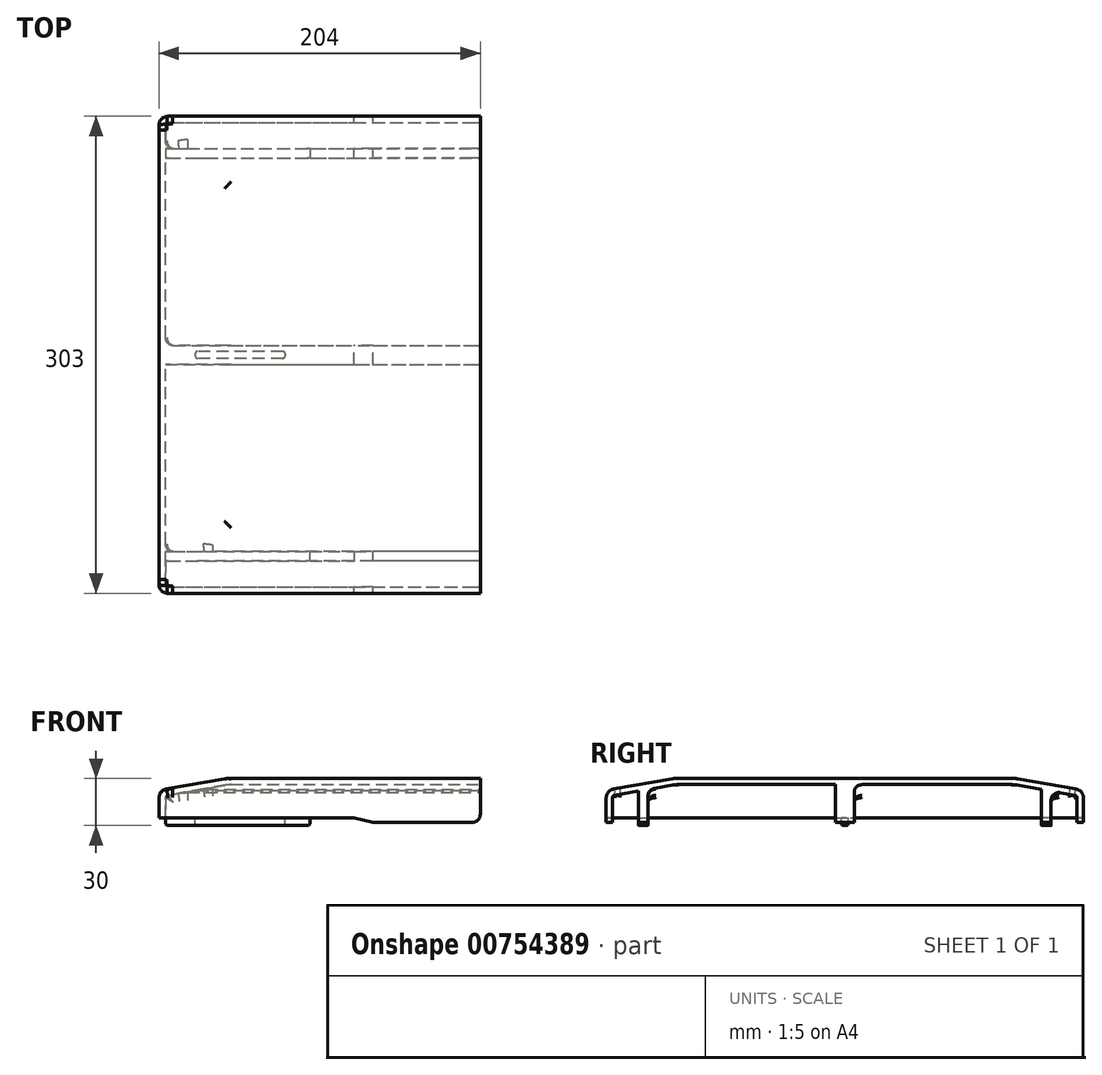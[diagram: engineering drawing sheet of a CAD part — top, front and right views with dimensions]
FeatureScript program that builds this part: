
annotation { "Feature Type Name" : "Feature", "Feature Type Description" : "" }
export const myFeature = defineFeature(function(context is Context, id is Id, definition is map)
    precondition{}
    {
        {
            var Q0;
            Q0=qCreatedBy(makeId("Front.planeOp"),FACE);
            var sketch = newSketch(context, id + "F0", { "sketchPlane" : qUnion([Q0])});
            skLineSegment(sketch, "E0.bottom", {"start": v(0, 0) * mm, "end": v(200, 0) * mm});
            skLineSegment(sketch, "E0.top", {"start": v(0, 21) * mm, "end": v(200, 21) * mm});
            skLineSegment(sketch, "E0.left", {"start": v(0, 0) * mm, "end": v(0, 21) * mm});
            skLineSegment(sketch, "E0.right", {"start": v(200, 0) * mm, "end": v(200, 21) * mm});
            skSolve(sketch);
        }
        {
            var Q0;
            Q0=makeQuery(id+"F0.imprint","IMPRINT",FACE,{"disambiguationData":[TD([[makeQuery(id+"F0.imprint","IMPRINT",EDGE,{"derivedFrom":sQuery(id+"F0.wireOp",EDGE,"E0.bottom")}),1.0]])]});
            extrude(context, id + "F1", {"entities" : qUnion([Q0]), "endBound" : BoundingType.SYMMETRIC, "depth" : 295 * mm, "offsetDistance" : 25 * mm});
        }
        {
            var Q0;
            Q0=makeQuery(id+"F1.opExtrude","CAP_EDGE",EDGE,{"disambiguationData":[OSD([sQuery(id+"F0.wireOp",EDGE,"E0.top")])],"isStart":false});
            var Q1;
            Q1=makeQuery(id+"F1.opExtrude","SWEPT_EDGE",EDGE,{"disambiguationData":[OSD([sQuery(id+"F0.wireOp",EDGE,"E0.top"),sQuery(id+"F0.wireOp",EDGE,"E0.left")])]});
            var Q2;
            Q2=makeQuery(id+"F1.opExtrude","CAP_EDGE",EDGE,{"disambiguationData":[OSD([sQuery(id+"F0.wireOp",EDGE,"E0.top")])],"isStart":true});
            chamfer(context, id + "F2", {"entities" : qUnion([Q0, Q1, Q2]), "chamferType" : ChamferType.TWO_OFFSETS, "width1" : 40 * mm, "oppositeDirection" : false, "width2" : 7 * mm, "tangentPropagation" : true});
        }
        {
            var Q0;
            {var subQ0=sQuery(id+"F0.wireOp",EDGE,"E0.top");Q0=makeQuery(id+"F2.opChamfer","BLEND_EDGE",EDGE,{"blendedFrom":[makeQuery(id+"F1.opExtrude","CAP_EDGE",EDGE,{"disambiguationData":[OSD([subQ0])],"isStart":false}),makeQuery(id+"F1.opExtrude","SWEPT_FACE",FACE,{"disambiguationData":[OSD([subQ0])]})],"blendedInto":[makeQuery(id+"F1.opExtrude","SWEPT_FACE",FACE,{"disambiguationData":[OSD([subQ0])]})]});}
            var Q1;
            {var subQ0=sQuery(id+"F0.wireOp",EDGE,"E0.top");Q1=makeQuery(id+"F2.opChamfer","BLEND_EDGE",EDGE,{"blendedFrom":[makeQuery(id+"F1.opExtrude","CAP_EDGE",EDGE,{"disambiguationData":[OSD([subQ0])],"isStart":true}),makeQuery(id+"F1.opExtrude","SWEPT_FACE",FACE,{"disambiguationData":[OSD([subQ0])]})],"blendedInto":[makeQuery(id+"F1.opExtrude","SWEPT_FACE",FACE,{"disambiguationData":[OSD([subQ0])]})]});}
            var Q2;
            {var subQ0=sQuery(id+"F0.wireOp",EDGE,"E0.top");Q2=makeQuery(id+"F2.opChamfer","BLEND_EDGE",EDGE,{"blendedFrom":[makeQuery(id+"F1.opExtrude","SWEPT_EDGE",EDGE,{"disambiguationData":[OSD([subQ0,sQuery(id+"F0.wireOp",EDGE,"E0.left")])]}),makeQuery(id+"F1.opExtrude","CAP_EDGE",EDGE,{"disambiguationData":[OSD([subQ0])],"isStart":false})],"blendedInto":[]});}
            var Q3;
            {var subQ0=sQuery(id+"F0.wireOp",EDGE,"E0.top");Q3=makeQuery(id+"F2.opChamfer","BLEND_EDGE",EDGE,{"blendedFrom":[makeQuery(id+"F1.opExtrude","SWEPT_EDGE",EDGE,{"disambiguationData":[OSD([subQ0,sQuery(id+"F0.wireOp",EDGE,"E0.left")])]}),makeQuery(id+"F1.opExtrude","CAP_EDGE",EDGE,{"disambiguationData":[OSD([subQ0])],"isStart":true})],"blendedInto":[]});}
            var Q4;
            {var subQ0=sQuery(id+"F0.wireOp",EDGE,"E0.top");Q4=makeQuery(id+"F2.opChamfer","BLEND_EDGE",EDGE,{"blendedFrom":[makeQuery(id+"F1.opExtrude","SWEPT_EDGE",EDGE,{"disambiguationData":[OSD([subQ0,sQuery(id+"F0.wireOp",EDGE,"E0.left")])]}),makeQuery(id+"F1.opExtrude","SWEPT_FACE",FACE,{"disambiguationData":[OSD([subQ0])]})],"blendedInto":[makeQuery(id+"F1.opExtrude","SWEPT_FACE",FACE,{"disambiguationData":[OSD([subQ0])]})]});}
            fillet(context, id + "F3", {"entities" : qUnion([Q0, Q1, Q2, Q3, Q4]), "radius" : 20 * mm, "tangentPropagation" : true, "allowEdgeOverflow" : false});
        }
        {
            var Q0;
            Q0=makeQuery(id+"F1.opExtrude","CAP_EDGE",EDGE,{"disambiguationData":[OSD([sQuery(id+"F0.wireOp",EDGE,"E0.left")])],"isStart":false});
            var Q1;
            {var subQ0=sQuery(id+"F0.wireOp",EDGE,"E0.left");var subQ1=sQuery(id+"F0.wireOp",EDGE,"E0.top");Q1=makeQuery(id+"F3.opFillet","BLEND_EDGE",EDGE,{"blendedFrom":[makeQuery(id+"F2.opChamfer","BLEND_EDGE",EDGE,{"blendedFrom":[makeQuery(id+"F1.opExtrude","SWEPT_EDGE",EDGE,{"disambiguationData":[OSD([subQ1,subQ0])]}),makeQuery(id+"F1.opExtrude","CAP_EDGE",EDGE,{"disambiguationData":[OSD([subQ1])],"isStart":false})],"blendedInto":[]}),makeQuery(id+"F1.opExtrude","CAP_FACE",FACE,{"disambiguationData":[OSD([sQuery(id+"F0.wireOp",EDGE,"E0.bottom"),subQ1,subQ0,sQuery(id+"F0.wireOp",EDGE,"E0.right")])],"isStart":false})],"blendedInto":[makeQuery(id+"F1.opExtrude","CAP_FACE",FACE,{"disambiguationData":[OSD([sQuery(id+"F0.wireOp",EDGE,"E0.bottom"),subQ1,subQ0,sQuery(id+"F0.wireOp",EDGE,"E0.right")])],"isStart":false})]});}
            var Q2;
            {var subQ0=sQuery(id+"F0.wireOp",EDGE,"E0.left");Q2=makeQuery(id+"F2.opChamfer","BLEND_EDGE",EDGE,{"blendedFrom":[makeQuery(id+"F1.opExtrude","SWEPT_EDGE",EDGE,{"disambiguationData":[OSD([sQuery(id+"F0.wireOp",EDGE,"E0.top"),subQ0])]}),makeQuery(id+"F1.opExtrude","SWEPT_FACE",FACE,{"disambiguationData":[OSD([subQ0])]})],"blendedInto":[makeQuery(id+"F1.opExtrude","SWEPT_FACE",FACE,{"disambiguationData":[OSD([subQ0])]})]});}
            var Q3;
            Q3=makeQuery(id+"F1.opExtrude","CAP_EDGE",EDGE,{"disambiguationData":[OSD([sQuery(id+"F0.wireOp",EDGE,"E0.left")])],"isStart":true});
            var Q4;
            {var subQ0=sQuery(id+"F0.wireOp",EDGE,"E0.top");Q4=makeQuery(id+"F2.opChamfer","BLEND_EDGE",EDGE,{"blendedFrom":[makeQuery(id+"F1.opExtrude","CAP_EDGE",EDGE,{"disambiguationData":[OSD([subQ0])],"isStart":true}),makeQuery(id+"F1.opExtrude","CAP_FACE",FACE,{"disambiguationData":[OSD([sQuery(id+"F0.wireOp",EDGE,"E0.bottom"),subQ0,sQuery(id+"F0.wireOp",EDGE,"E0.left"),sQuery(id+"F0.wireOp",EDGE,"E0.right")])],"isStart":true})],"blendedInto":[makeQuery(id+"F1.opExtrude","CAP_FACE",FACE,{"disambiguationData":[OSD([sQuery(id+"F0.wireOp",EDGE,"E0.bottom"),subQ0,sQuery(id+"F0.wireOp",EDGE,"E0.left"),sQuery(id+"F0.wireOp",EDGE,"E0.right")])],"isStart":true})]});}
            fillet(context, id + "F4", {"entities" : qUnion([Q0, Q1, Q2, Q3, Q4]), "radius" : 1.5 * mm, "tangentPropagation" : true, "allowEdgeOverflow" : false});
        }
        {
            var Q0;
            Q0=makeQuery(id+"F1.opExtrude","SWEPT_FACE",FACE,{"disambiguationData":[OSD([sQuery(id+"F0.wireOp",EDGE,"E0.bottom")])]});
            var Q1;
            Q1=makeQuery(id+"F1.opExtrude","SWEPT_FACE",FACE,{"disambiguationData":[OSD([sQuery(id+"F0.wireOp",EDGE,"E0.right")])]});
            shell(context, id + "F5", {"entities" : qUnion([Q0, Q1]), "thickness" : 4 * mm, "oppositeDirection" : true});
        }
        {
            var Q0;
            Q0=makeQuery(id+"F0.imprint","IMPRINT",FACE,{"disambiguationData":[TD([[makeQuery(id+"F0.imprint","IMPRINT",EDGE,{"derivedFrom":sQuery(id+"F0.wireOp",EDGE,"E0.bottom")}),1.0]])]});
            extrude(context, id + "F6", {"entities" : qUnion([Q0]), "operationType" : NewBodyOperationType.ADD, "endBound" : BoundingType.SYMMETRIC, "depth" : 12 * mm, "offsetDistance" : 25 * mm});
        }
        {
            var Q0;
            {var subQ0=sQuery(id+"F0.wireOp",EDGE,"E0.left");var subQ1=sQuery(id+"F0.wireOp",EDGE,"E0.top");Q0=makeQuery(id+"F6.boolean.opBoolean","SPLIT",FACE,{"disambiguationData":[TD([makeQuery(id+"F6.opExtrude","SWEPT_FACE",FACE,{"disambiguationData":[OSD([subQ1])]})])],"derivedFrom":makeQuery(id+"F6.opExtrude","CAP_FACE",FACE,{"disambiguationData":[OSD([sQuery(id+"F0.wireOp",EDGE,"E0.bottom"),subQ1,subQ0,sQuery(id+"F0.wireOp",EDGE,"E0.right")])],"isStart":false})});}
            extrude(context, id + "F7", {"entities" : qUnion([Q0]), "operationType" : NewBodyOperationType.REMOVE, "oppositeDirection" : true, "depth" : 25 * mm, "offsetDistance" : 25 * mm});
        }
        {
            var Q0;
            {var subQ0=sQuery(id+"F0.wireOp",EDGE,"E0.top");Q0=makeQuery(id+"F6.boolean.opBoolean","SPLIT",EDGE,{"disambiguationData":[topologyDisambiguationEdgeConnected([makeQuery(id+"F5.opShell","OFFSET_FACE",FACE,{"disambiguationData":[OSD([subQ0]),TDD([makeQuery(id+"F1.opExtrude","SWEPT_FACE",FACE,{"disambiguationData":[OSD([subQ0])]})])]})])],"derivedFrom":makeQuery(id+"F6.opExtrude","CAP_EDGE",EDGE,{"disambiguationData":[OSD([subQ0])],"isStart":false})});}
            var Q1;
            {var subQ0=sQuery(id+"F0.wireOp",EDGE,"E0.top");Q1=makeQuery(id+"F6.boolean.opBoolean","SPLIT",EDGE,{"disambiguationData":[topologyDisambiguationEdgeConnected([makeQuery(id+"F5.opShell","OFFSET_FACE",FACE,{"disambiguationData":[OSD([subQ0]),TDD([makeQuery(id+"F1.opExtrude","SWEPT_FACE",FACE,{"disambiguationData":[OSD([subQ0])]})])]})])],"derivedFrom":makeQuery(id+"F6.opExtrude","CAP_EDGE",EDGE,{"disambiguationData":[OSD([subQ0])],"isStart":true})});}
            fillet(context, id + "F8", {"entities" : qUnion([Q0, Q1]), "radius" : 5 * mm, "tangentPropagation" : true, "allowEdgeOverflow" : false});
        }
        {
            var Q0;
            {var subQ0=sQuery(id+"F0.wireOp",EDGE,"E0.bottom");Q0=makeQuery(id+"F6.boolean.opBoolean","MERGE",FACE,{"derivedFrom":[makeQuery(id+"F1.opExtrude","SWEPT_FACE",FACE,{"disambiguationData":[OSD([subQ0])]}),makeQuery(id+"F6.opExtrude","SWEPT_FACE",FACE,{"disambiguationData":[OSD([subQ0])]})]});}
            var sketch = newSketch(context, id + "F9", { "sketchPlane" : qUnion([Q0])});
            skLineSegment(sketch, "E1.bottom", {"start": v(76, -2.25) * mm, "end": v(19, -2.25) * mm});
            skLineSegment(sketch, "E1.top", {"start": v(76, 2.25) * mm, "end": v(19, 2.25) * mm});
            skLineSegment(sketch, "E1.left", {"start": v(76, -2.25) * mm, "end": v(76, 2.25) * mm});
            skLineSegment(sketch, "E1.right", {"start": v(19, -2.25) * mm, "end": v(19, 2.25) * mm});
            skPoint(sketch, "E1.middle", {"position": v(47.5, 0) * mm});
            skSolve(sketch);
        }
        {
            var Q0;
            Q0=makeQuery(id+"F9.imprint","IMPRINT",FACE,{"disambiguationData":[TD([[makeQuery(id+"F9.imprint","IMPRINT",EDGE,{"derivedFrom":sQuery(id+"F9.wireOp",EDGE,"E1.bottom")}),-1.0]])]});
            extrude(context, id + "F10", {"entities" : qUnion([Q0]), "operationType" : NewBodyOperationType.ADD, "depth" : 5 * mm, "offsetDistance" : 25 * mm});
        }
        {
            var Q0;
            Q0=makeQuery(id+"F10.opExtrude","CAP_FACE",FACE,{"disambiguationData":[OSD([sQuery(id+"F9.wireOp",EDGE,"E1.bottom"),sQuery(id+"F9.wireOp",EDGE,"E1.top"),sQuery(id+"F9.wireOp",EDGE,"E1.left"),sQuery(id+"F9.wireOp",EDGE,"E1.right")])],"isStart":false});
            var Q1;
            Q1=makeQuery(id+"F10.opExtrude","SWEPT_EDGE",EDGE,{"disambiguationData":[OSD([sQuery(id+"F9.wireOp",EDGE,"E1.bottom"),sQuery(id+"F9.wireOp",EDGE,"E1.left")])]});
            var Q2;
            Q2=makeQuery(id+"F10.opExtrude","SWEPT_EDGE",EDGE,{"disambiguationData":[OSD([sQuery(id+"F9.wireOp",EDGE,"E1.top"),sQuery(id+"F9.wireOp",EDGE,"E1.left")])]});
            var Q3;
            Q3=makeQuery(id+"F10.opExtrude","SWEPT_EDGE",EDGE,{"disambiguationData":[OSD([sQuery(id+"F9.wireOp",EDGE,"E1.top"),sQuery(id+"F9.wireOp",EDGE,"E1.right")])]});
            var Q4;
            Q4=makeQuery(id+"F10.opExtrude","SWEPT_EDGE",EDGE,{"disambiguationData":[OSD([sQuery(id+"F9.wireOp",EDGE,"E1.bottom"),sQuery(id+"F9.wireOp",EDGE,"E1.right")])]});
            fillet(context, id + "F11", {"entities" : qUnion([Q0, Q1, Q2, Q3, Q4]), "radius" : 1.5 * mm, "tangentPropagation" : true, "allowEdgeOverflow" : false});
        }
        {
            var Q0;
            Q0=qCreatedBy(makeId("Top.planeOp"),FACE);
            var sketch = newSketch(context, id + "F12", { "sketchPlane" : qUnion([Q0])});
            skLineSegment(sketch, "E2.bottom", {"start": v(0, -131) * mm, "end": v(92, -131) * mm});
            skLineSegment(sketch, "E2.top", {"start": v(0, -125) * mm, "end": v(92, -125) * mm});
            skLineSegment(sketch, "E2.left", {"start": v(0, -131) * mm, "end": v(0, -125) * mm});
            skLineSegment(sketch, "E2.right", {"start": v(92, -131) * mm, "end": v(92, -125) * mm});
            skLineSegment(sketch, "E3.MirrorCS", {"start": v(0, 131) * mm, "end": v(0, 125) * mm});
            skLineSegment(sketch, "E4.MirrorCS", {"start": v(92, 131) * mm, "end": v(92, 125) * mm});
            skLineSegment(sketch, "E5.MirrorCS", {"start": v(0, 131) * mm, "end": v(92, 131) * mm});
            skLineSegment(sketch, "E6.MirrorCS", {"start": v(0, 125) * mm, "end": v(92, 125) * mm});
            skLineSegment(sketch, "E7.bottom", {"start": v(92, -131) * mm, "end": v(200, -131) * mm});
            skLineSegment(sketch, "E7.top", {"start": v(92, -125) * mm, "end": v(200, -125) * mm});
            skLineSegment(sketch, "E7.right", {"start": v(200, -131) * mm, "end": v(200, -125) * mm});
            skLineSegment(sketch, "E8.MirrorCS", {"start": v(92, 131) * mm, "end": v(200, 131) * mm});
            skLineSegment(sketch, "E9.MirrorCS", {"start": v(92, 125) * mm, "end": v(200, 125) * mm});
            skLineSegment(sketch, "E10.MirrorCS", {"start": v(200, 131) * mm, "end": v(200, 125) * mm});
            skSolve(sketch);
        }
        {
            var Q0;
            Q0=makeQuery(id+"F12.imprint","IMPRINT",FACE,{"disambiguationData":[TD([[makeQuery(id+"F12.imprint","IMPRINT",EDGE,{"derivedFrom":sQuery(id+"F12.wireOp",EDGE,"E2.bottom")}),1.0]])]});
            var Q1;
            Q1=makeQuery(id+"F12.imprint","IMPRINT",FACE,{"disambiguationData":[TD([[makeQuery(id+"F12.imprint","IMPRINT",EDGE,{"derivedFrom":sQuery(id+"F12.wireOp",EDGE,"E7.bottom")}),1.0]])]});
            var Q2;
            {var subQ0=sQuery(id+"F0.wireOp",EDGE,"E0.top");Q2=makeQuery(id+"F5.opShell","OFFSET_FACE",FACE,{"disambiguationData":[OSD([subQ0]),TDD([makeQuery(id+"F2.opChamfer","BLEND_FACE",FACE,{"disambiguationData":[OSD([subQ0]),TDD([makeQuery(id+"F1.opExtrude","CAP_EDGE",EDGE,{"disambiguationData":[OSD([subQ0])],"isStart":false})])]})])]});}
            extrude(context, id + "F13", {"entities" : qUnion([Q0, Q1]), "operationType" : NewBodyOperationType.ADD, "endBound" : BoundingType.UP_TO_SURFACE, "depth" : 25 * mm, "endBoundEntityFace" : qUnion([Q2]), "offsetDistance" : 25 * mm});
        }
        {
            var Q0;
            Q0=makeQuery(id+"F12.imprint","IMPRINT",FACE,{"disambiguationData":[TD([[makeQuery(id+"F12.imprint","IMPRINT",EDGE,{"derivedFrom":sQuery(id+"F12.wireOp",EDGE,"E3.MirrorCS")}),1.0]])]});
            var Q1;
            Q1=makeQuery(id+"F12.imprint","IMPRINT",FACE,{"disambiguationData":[TD([[makeQuery(id+"F12.imprint","IMPRINT",EDGE,{"derivedFrom":sQuery(id+"F12.wireOp",EDGE,"E4.MirrorCS")}),1.0]])]});
            var Q2;
            {var subQ0=sQuery(id+"F0.wireOp",EDGE,"E0.top");Q2=makeQuery(id+"F5.opShell","OFFSET_FACE",FACE,{"disambiguationData":[OSD([subQ0]),TDD([makeQuery(id+"F2.opChamfer","BLEND_FACE",FACE,{"disambiguationData":[OSD([subQ0]),TDD([makeQuery(id+"F1.opExtrude","CAP_EDGE",EDGE,{"disambiguationData":[OSD([subQ0])],"isStart":true})])]})])]});}
            extrude(context, id + "F14", {"entities" : qUnion([Q0, Q1]), "operationType" : NewBodyOperationType.ADD, "endBound" : BoundingType.UP_TO_SURFACE, "depth" : 25 * mm, "endBoundEntityFace" : qUnion([Q2]), "offsetDistance" : 25 * mm});
        }
        {
            var Q0;
            Q0=makeQuery(id+"F12.imprint","IMPRINT",FACE,{"disambiguationData":[TD([[makeQuery(id+"F12.imprint","IMPRINT",EDGE,{"derivedFrom":sQuery(id+"F12.wireOp",EDGE,"E2.bottom")}),1.0]])]});
            var Q1;
            Q1=makeQuery(id+"F12.imprint","IMPRINT",FACE,{"disambiguationData":[TD([[makeQuery(id+"F12.imprint","IMPRINT",EDGE,{"derivedFrom":sQuery(id+"F12.wireOp",EDGE,"E3.MirrorCS")}),1.0]])]});
            extrude(context, id + "F15", {"entities" : qUnion([Q0, Q1]), "operationType" : NewBodyOperationType.ADD, "oppositeDirection" : true, "depth" : 5 * mm, "offsetDistance" : 25 * mm});
        }
        {
            var Q0;
            Q0=makeQuery(id+"F15.opExtrude","CAP_EDGE",EDGE,{"disambiguationData":[OSD([sQuery(id+"F12.wireOp",EDGE,"E2.right")])],"isStart":false});
            var Q1;
            Q1=makeQuery(id+"F15.opExtrude","CAP_EDGE",EDGE,{"disambiguationData":[OSD([sQuery(id+"F12.wireOp",EDGE,"E2.left")])],"isStart":false});
            var Q2;
            Q2=makeQuery(id+"F15.opExtrude","CAP_EDGE",EDGE,{"disambiguationData":[OSD([sQuery(id+"F12.wireOp",EDGE,"E4.MirrorCS")])],"isStart":false});
            var Q3;
            Q3=makeQuery(id+"F15.opExtrude","CAP_EDGE",EDGE,{"disambiguationData":[OSD([sQuery(id+"F12.wireOp",EDGE,"E3.MirrorCS")])],"isStart":false});
            fillet(context, id + "F16", {"entities" : qUnion([Q0, Q1, Q2, Q3]), "radius" : 2 * mm, "tangentPropagation" : true, "allowEdgeOverflow" : false});
        }
        {
            var Q0;
            Q0=makeQuery(id+"F13.opExtrude","CAP_EDGE",EDGE,{"disambiguationData":[OSD([sQuery(id+"F12.wireOp",EDGE,"E2.bottom"),sQuery(id+"F12.wireOp",EDGE,"E7.bottom")])],"isStart":false});
            var Q1;
            Q1=makeQuery(id+"F13.opExtrude","CAP_EDGE",EDGE,{"disambiguationData":[OSD([sQuery(id+"F12.wireOp",EDGE,"E2.top"),sQuery(id+"F12.wireOp",EDGE,"E7.top")])],"isStart":false});
            var Q2;
            Q2=makeQuery(id+"F14.opExtrude","CAP_EDGE",EDGE,{"disambiguationData":[OSD([sQuery(id+"F12.wireOp",EDGE,"E5.MirrorCS"),sQuery(id+"F12.wireOp",EDGE,"E8.MirrorCS")])],"isStart":false});
            var Q3;
            Q3=makeQuery(id+"F14.opExtrude","CAP_EDGE",EDGE,{"disambiguationData":[OSD([sQuery(id+"F12.wireOp",EDGE,"E6.MirrorCS"),sQuery(id+"F12.wireOp",EDGE,"E9.MirrorCS")])],"isStart":false});
            fillet(context, id + "F17", {"entities" : qUnion([Q0, Q1, Q2, Q3]), "radius" : 5 * mm, "tangentPropagation" : true, "allowEdgeOverflow" : false});
        }
        {
            var Q0;
            {var subQ3=sQuery(id+"F0.wireOp",EDGE,"E0.left");var subQ7=sQuery(id+"F12.wireOp",EDGE,"E6.MirrorCS");var subQ8=makeQuery(id+"F1.opExtrude","SWEPT_FACE",FACE,{"disambiguationData":[OSD([subQ3])]});var subQ12=sQuery(id+"F0.wireOp",EDGE,"E0.bottom");var subQ15=sQuery(id+"F12.wireOp",EDGE,"E7.bottom");var subQ16=sQuery(id+"F12.wireOp",EDGE,"E2.bottom");var subQ19=sQuery(id+"F12.wireOp",EDGE,"E7.top");var subQ20=sQuery(id+"F12.wireOp",EDGE,"E2.top");var subQ21=sQuery(id+"F12.wireOp",EDGE,"E8.MirrorCS");var subQ22=sQuery(id+"F12.wireOp",EDGE,"E5.MirrorCS");var subQ23=sQuery(id+"F12.wireOp",EDGE,"E9.MirrorCS");var subQ24=sQuery(id+"F12.wireOp",EDGE,"E2.left");var subQ25=sQuery(id+"F12.wireOp",EDGE,"E3.MirrorCS");Q0=makeQuery(id+"F15.boolean.opBoolean","SPLIT",FACE,{"disambiguationData":[TD([subQ8])],"derivedFrom":makeQuery(id+"F14.boolean.opBoolean","MERGE",FACE,{"derivedFrom":[makeQuery(id+"F13.boolean.opBoolean","MERGE",FACE,{"derivedFrom":[makeQuery(id+"F6.boolean.opBoolean","MERGE",FACE,{"derivedFrom":[makeQuery(id+"F1.opExtrude","SWEPT_FACE",FACE,{"disambiguationData":[OSD([subQ12])]}),makeQuery(id+"F6.opExtrude","SWEPT_FACE",FACE,{"disambiguationData":[OSD([subQ12])]})]}),makeQuery(id+"F13.opExtrude","CAP_FACE",FACE,{"disambiguationData":[OSD([subQ16,subQ20,subQ24,subQ15,subQ19,sQuery(id+"F12.wireOp",EDGE,"E7.right")])],"isStart":true})]}),makeQuery(id+"F14.opExtrude","CAP_FACE",FACE,{"disambiguationData":[OSD([subQ25,subQ22,subQ7,subQ21,subQ23,sQuery(id+"F12.wireOp",EDGE,"E10.MirrorCS")])],"isStart":true})]})});}
            var sketch = newSketch(context, id + "F18", { "sketchPlane" : qUnion([Q0])});
            skLineSegment(sketch, "E11.bottom", {"start": v(200, 6) * mm, "end": v(120, 6) * mm});
            skLineSegment(sketch, "E11.top", {"start": v(200, -6) * mm, "end": v(120, -6) * mm});
            skLineSegment(sketch, "E11.left", {"start": v(200, 6) * mm, "end": v(200, -6) * mm});
            skLineSegment(sketch, "E11.right", {"start": v(120, 6) * mm, "end": v(120, -6) * mm});
            skLineSegment(sketch, "E12.bottom", {"start": v(200, 125) * mm, "end": v(120, 125) * mm});
            skLineSegment(sketch, "E12.top", {"start": v(200, 131) * mm, "end": v(120, 131) * mm});
            skLineSegment(sketch, "E12.left", {"start": v(200, 125) * mm, "end": v(200, 131) * mm});
            skLineSegment(sketch, "E12.right", {"start": v(120, 125) * mm, "end": v(120, 131) * mm});
            skLineSegment(sketch, "E13.MirrorCS", {"start": v(200, -125) * mm, "end": v(120, -125) * mm});
            skLineSegment(sketch, "E14.MirrorCS", {"start": v(200, -131) * mm, "end": v(120, -131) * mm});
            skLineSegment(sketch, "E15.MirrorCS", {"start": v(200, -125) * mm, "end": v(200, -131) * mm});
            skLineSegment(sketch, "E16.MirrorCS", {"start": v(120, -125) * mm, "end": v(120, -131) * mm});
            skLineSegment(sketch, "E17.bottom", {"start": v(200, 151.5) * mm, "end": v(120, 151.5) * mm});
            skLineSegment(sketch, "E17.top", {"start": v(200, 147.5) * mm, "end": v(120, 147.5) * mm});
            skLineSegment(sketch, "E17.left", {"start": v(200, 151.5) * mm, "end": v(200, 147.5) * mm});
            skLineSegment(sketch, "E17.right", {"start": v(120, 151.5) * mm, "end": v(120, 147.5) * mm});
            skLineSegment(sketch, "E18.bottom", {"start": v(200, -147.5) * mm, "end": v(120, -147.5) * mm});
            skLineSegment(sketch, "E18.top", {"start": v(200, -151.5) * mm, "end": v(120, -151.5) * mm});
            skLineSegment(sketch, "E18.left", {"start": v(200, -147.5) * mm, "end": v(200, -151.5) * mm});
            skLineSegment(sketch, "E18.right", {"start": v(120, -147.5) * mm, "end": v(120, -151.5) * mm});
            skSolve(sketch);
        }
        {
            var Q0;
            Q0=makeQuery(id+"F18.imprint","IMPRINT",FACE,{"disambiguationData":[TD([[makeQuery(id+"F18.imprint","IMPRINT",EDGE,{"derivedFrom":sQuery(id+"F18.wireOp",EDGE,"E17.bottom")}),-1.0]])]});
            var Q1;
            Q1=makeQuery(id+"F18.imprint","IMPRINT",FACE,{"disambiguationData":[TD([[makeQuery(id+"F18.imprint","IMPRINT",EDGE,{"derivedFrom":sQuery(id+"F18.wireOp",EDGE,"E12.bottom")}),-1.0]])]});
            var Q2;
            Q2=makeQuery(id+"F18.imprint","IMPRINT",FACE,{"disambiguationData":[TD([[makeQuery(id+"F18.imprint","IMPRINT",EDGE,{"derivedFrom":sQuery(id+"F18.wireOp",EDGE,"E11.bottom")}),-1.0]])]});
            var Q3;
            Q3=makeQuery(id+"F18.imprint","IMPRINT",FACE,{"disambiguationData":[TD([[makeQuery(id+"F18.imprint","IMPRINT",EDGE,{"derivedFrom":sQuery(id+"F18.wireOp",EDGE,"E13.MirrorCS")}),1.0]])]});
            var Q4;
            Q4=makeQuery(id+"F18.imprint","IMPRINT",FACE,{"disambiguationData":[TD([[makeQuery(id+"F18.imprint","IMPRINT",EDGE,{"derivedFrom":sQuery(id+"F18.wireOp",EDGE,"E18.bottom")}),-1.0]])]});
            extrude(context, id + "F19", {"entities" : qUnion([Q0, Q1, Q2, Q3, Q4]), "operationType" : NewBodyOperationType.ADD, "depth" : 3 * mm, "offsetDistance" : 25 * mm});
        }
        {
            var Q0;
            Q0=makeQuery(id+"F19.opExtrude","CAP_EDGE",EDGE,{"disambiguationData":[OSD([sQuery(id+"F18.wireOp",EDGE,"E17.right")])],"isStart":false});
            var Q1;
            Q1=makeQuery(id+"F19.opExtrude","CAP_EDGE",EDGE,{"disambiguationData":[OSD([sQuery(id+"F18.wireOp",EDGE,"E11.right")])],"isStart":false});
            var Q2;
            Q2=makeQuery(id+"F19.opExtrude","CAP_EDGE",EDGE,{"disambiguationData":[OSD([sQuery(id+"F18.wireOp",EDGE,"E16.MirrorCS")])],"isStart":false});
            var Q3;
            Q3=makeQuery(id+"F19.opExtrude","CAP_EDGE",EDGE,{"disambiguationData":[OSD([sQuery(id+"F18.wireOp",EDGE,"E18.right")])],"isStart":false});
            chamfer(context, id + "F20", {"entities" : qUnion([Q0, Q1, Q2, Q3]), "chamferType" : ChamferType.TWO_OFFSETS, "width1" : 3 * mm, "oppositeDirection" : true, "width2" : 12 * mm, "tangentPropagation" : true});
        }
        {
            var Q0;
            Q0=makeQuery(id+"F19.opExtrude","CAP_EDGE",EDGE,{"disambiguationData":[OSD([sQuery(id+"F18.wireOp",EDGE,"E12.right")])],"isStart":false});
            chamfer(context, id + "F21", {"entities" : qUnion([Q0]), "chamferType" : ChamferType.TWO_OFFSETS, "width1" : 3 * mm, "oppositeDirection" : false, "width2" : 12 * mm, "tangentPropagation" : true});
        }
        {
            var Q0;
            Q0=makeQuery(id+"F19.opExtrude","CAP_EDGE",EDGE,{"disambiguationData":[OSD([sQuery(id+"F18.wireOp",EDGE,"E17.left")])],"isStart":false});
            var Q1;
            Q1=makeQuery(id+"F19.opExtrude","CAP_EDGE",EDGE,{"disambiguationData":[OSD([sQuery(id+"F18.wireOp",EDGE,"E12.left")])],"isStart":false});
            var Q2;
            Q2=makeQuery(id+"F19.opExtrude","CAP_EDGE",EDGE,{"disambiguationData":[OSD([sQuery(id+"F18.wireOp",EDGE,"E11.left")])],"isStart":false});
            var Q3;
            Q3=makeQuery(id+"F19.opExtrude","CAP_EDGE",EDGE,{"disambiguationData":[OSD([sQuery(id+"F18.wireOp",EDGE,"E15.MirrorCS")])],"isStart":false});
            var Q4;
            Q4=makeQuery(id+"F19.opExtrude","CAP_EDGE",EDGE,{"disambiguationData":[OSD([sQuery(id+"F18.wireOp",EDGE,"E18.left")])],"isStart":false});
            fillet(context, id + "F22", {"entities" : qUnion([Q0, Q1, Q2, Q3, Q4]), "radius" : 5 * mm, "tangentPropagation" : true, "allowEdgeOverflow" : false});
        }
    });
